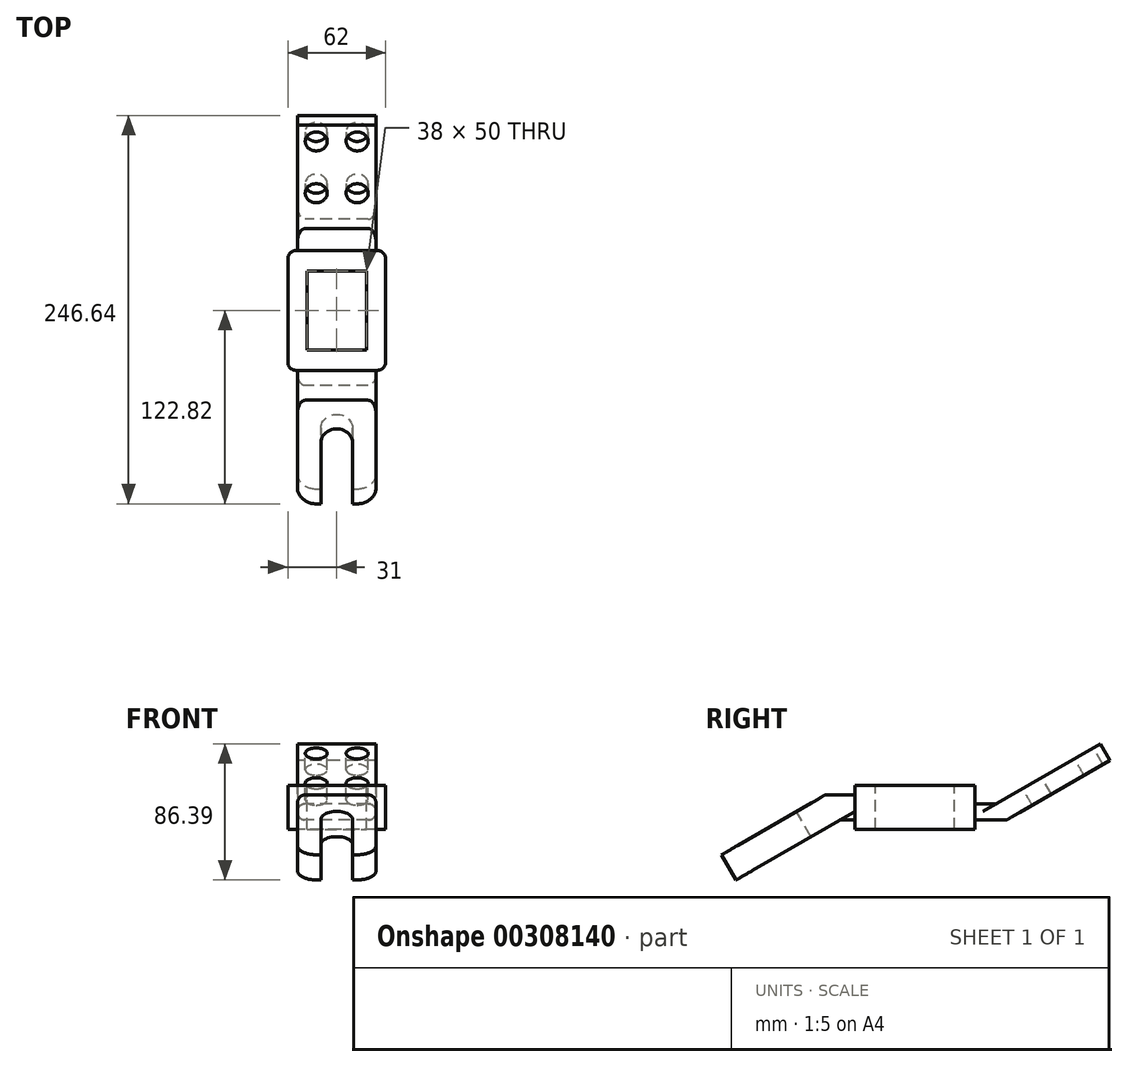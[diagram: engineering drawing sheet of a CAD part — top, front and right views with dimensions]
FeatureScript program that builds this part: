
annotation { "Feature Type Name" : "Feature", "Feature Type Description" : "" }
export const myFeature = defineFeature(function(context is Context, id is Id, definition is map)
    precondition{}
    {
        {
            var Q0;
            Q0=qCreatedBy(makeId("Right.planeOp"),FACE);
            var sketch = newSketch(context, id + "F0", { "sketchPlane" : qUnion([Q0])});
            skLineSegment(sketch, "E0.bottom", {"start": v(38, 14) * mm, "end": v(-38, 14) * mm});
            skLineSegment(sketch, "E0.top", {"start": v(38, -14) * mm, "end": v(-38, -14) * mm});
            skLineSegment(sketch, "E0.left", {"start": v(38, 14) * mm, "end": v(38, -14) * mm});
            skLineSegment(sketch, "E0.right", {"start": v(-38, 14) * mm, "end": v(-38, -14) * mm});
            skPoint(sketch, "E0.middle", {"position": v(0, 0) * mm});
            skLineSegment(sketch, "E1", {"start": v(-38, 8) * mm, "end": v(-57, 8) * mm});
            skLineSegment(sketch, "E2", {"start": v(-57, 8) * mm, "end": v(-122.82, -30) * mm});
            skLineSegment(sketch, "E3", {"start": v(-122.82, -30) * mm, "end": v(-113.58, -46) * mm});
            skLineSegment(sketch, "E4", {"start": v(38, -8) * mm, "end": v(58, -8) * mm});
            skLineSegment(sketch, "E5", {"start": v(58, -8) * mm, "end": v(123.82, 30) * mm});
            skLineSegment(sketch, "E6", {"start": v(123.82, 30) * mm, "end": v(117.82, 40.4) * mm});
            skLineSegment(sketch, "E7", {"start": v(117.82, 40.4) * mm, "end": v(52, 2.4) * mm});
            skLineSegment(sketch, "E8", {"start": v(-38, -8) * mm, "end": v(-47.76, -8) * mm});
            skLineSegment(sketch, "E9", {"start": v(-47.76, -8) * mm, "end": v(-113.58, -46) * mm});
            skLineSegment(sketch, "E10", {"start": v(52, 2.4) * mm, "end": v(38, 2.4) * mm});
            skSolve(sketch);
        }
        {
            var Q0;
            {var subQ3=sQuery(id+"F0.wireOp",EDGE,"E0.bottom");Q0=makeQuery(id+"F0.imprint","IMPRINT",FACE,{"disambiguationData":[TD([[makeQuery(id+"F0.imprint","IMPRINT",EDGE,{"derivedFrom":subQ3}),1.0]])]});}
            extrude(context, id + "F1", {"entities" : qUnion([Q0]), "endBound" : BoundingType.SYMMETRIC, "depth" : 62 * mm});
        }
        {
            var Q0;
            {var subQ0=sQuery(id+"F0.wireOp",EDGE,"E1");Q0=makeQuery(id+"F0.imprint","IMPRINT",FACE,{"disambiguationData":[TD([[makeQuery(id+"F0.imprint","IMPRINT",EDGE,{"derivedFrom":subQ0}),1.0]])]});}
            var Q1;
            {var subQ0=sQuery(id+"F0.wireOp",EDGE,"E4");Q1=makeQuery(id+"F0.imprint","IMPRINT",FACE,{"disambiguationData":[TD([[makeQuery(id+"F0.imprint","IMPRINT",EDGE,{"derivedFrom":subQ0}),1.0]])]});}
            extrude(context, id + "F2", {"entities" : qUnion([Q0, Q1]), "operationType" : NewBodyOperationType.ADD, "endBound" : BoundingType.SYMMETRIC, "depth" : 50 * mm});
        }
        {
            var Q0;
            Q0=makeQuery(id+"F2.opExtrude","SWEPT_FACE",FACE,{"disambiguationData":[OSD([sQuery(id+"F0.wireOp",EDGE,"E2")])]});
            var sketch = newSketch(context, id + "F3", { "sketchPlane" : qUnion([Q0])});
            skCircle(sketch, "E11", {"center": v(0, -76.36) * mm, "radius": 10 * mm});
            skLineSegment(sketch, "E12", {"start": v(-10, -76.36) * mm, "end": v(-10, -121.36) * mm});
            skLineSegment(sketch, "E13", {"start": v(10, -76.36) * mm, "end": v(10, -121.36) * mm});
            skSolve(sketch);
        }
        {
            var Q0;
            {var subQ0=sQuery(id+"F3.wireOp",EDGE,"E12");Q0=makeQuery(id+"F3.imprint","IMPRINT",FACE,{"disambiguationData":[TD([[makeQuery(id+"F3.imprint","IMPRINT",EDGE,{"derivedFrom":subQ0}),1.0]])]});}
            var Q1;
            {var subQ0=sQuery(id+"F3.wireOp",EDGE,"E11");var subQ1=makeQuery(id+"F3.imprint","INTERSECT",VERTEX,{"derivedFrom":[subQ0,sQuery(id+"F3.wireOp",EDGE,"E12")]});Q1=makeQuery(id+"F3.imprint","IMPRINT",FACE,{"disambiguationData":[TD([[makeQuery(id+"F3.imprint","IMPRINT",EDGE,{"disambiguationData":[TD([[subQ1,1.0]])],"derivedFrom":subQ0}),1.0]])]});}
            extrude(context, id + "F4", {"entities" : qUnion([Q0, Q1]), "operationType" : NewBodyOperationType.REMOVE, "endBound" : BoundingType.THROUGH_ALL, "oppositeDirection" : true, "depth" : 25 * mm});
        }
        {
            var Q0;
            Q0=makeQuery(id+"F2.opExtrude","CAP_EDGE",EDGE,{"disambiguationData":[OSD([sQuery(id+"F0.wireOp",EDGE,"E3")])],"isStart":false});
            var Q1;
            Q1=makeQuery(id+"F2.opExtrude","CAP_EDGE",EDGE,{"disambiguationData":[OSD([sQuery(id+"F0.wireOp",EDGE,"E3")])],"isStart":true});
            fillet(context, id + "F5", {"entities" : qUnion([Q0, Q1]), "radius" : 12 * mm, "tangentPropagation" : true, "allowEdgeOverflow" : false});
        }
        {
            var Q0;
            Q0=makeQuery(id+"F2.opExtrude","SWEPT_FACE",FACE,{"disambiguationData":[OSD([sQuery(id+"F0.wireOp",EDGE,"E7")])]});
            var sketch = newSketch(context, id + "F6", { "sketchPlane" : qUnion([Q0])});
            skCircle(sketch, "E14", {"center": v(-13, 110.23) * mm, "radius": 7 * mm});
            skCircle(sketch, "E15.0.1.0", {"center": v(-13, 72.23) * mm, "radius": 7 * mm});
            skCircle(sketch, "E15.1.0.0", {"center": v(13, 110.23) * mm, "radius": 7 * mm});
            skCircle(sketch, "E15.1.1.0", {"center": v(13, 72.23) * mm, "radius": 7 * mm});
            skLineSegment(sketch, "E15.direction1", {"start": v(-13, 110.23) * mm, "end": v(13, 110.23) * mm, "construction": true});
            skLineSegment(sketch, "E15.direction2", {"start": v(-13, 110.23) * mm, "end": v(-13, 72.23) * mm, "construction": true});
            skSolve(sketch);
        }
        {
            var Q0;
            Q0=makeQuery(id+"F6.imprint","IMPRINT",FACE,{"disambiguationData":[TD([[makeQuery(id+"F6.imprint","IMPRINT",EDGE,{"derivedFrom":sQuery(id+"F6.wireOp",EDGE,"E14")}),1.0]])]});
            var Q1;
            Q1=makeQuery(id+"F6.imprint","IMPRINT",FACE,{"disambiguationData":[TD([[makeQuery(id+"F6.imprint","IMPRINT",EDGE,{"derivedFrom":sQuery(id+"F6.wireOp",EDGE,"E15.1.0.0")}),1.0]])]});
            var Q2;
            Q2=makeQuery(id+"F6.imprint","IMPRINT",FACE,{"disambiguationData":[TD([[makeQuery(id+"F6.imprint","IMPRINT",EDGE,{"derivedFrom":sQuery(id+"F6.wireOp",EDGE,"E15.1.1.0")}),1.0]])]});
            var Q3;
            Q3=makeQuery(id+"F6.imprint","IMPRINT",FACE,{"disambiguationData":[TD([[makeQuery(id+"F6.imprint","IMPRINT",EDGE,{"derivedFrom":sQuery(id+"F6.wireOp",EDGE,"E15.0.1.0")}),1.0]])]});
            extrude(context, id + "F7", {"entities" : qUnion([Q0, Q1, Q2, Q3]), "operationType" : NewBodyOperationType.REMOVE, "endBound" : BoundingType.THROUGH_ALL, "oppositeDirection" : true, "depth" : 25 * mm});
        }
        {
            var Q0;
            Q0=makeQuery(id+"F1.opExtrude","SWEPT_FACE",FACE,{"disambiguationData":[OSD([sQuery(id+"F0.wireOp",EDGE,"E0.bottom")])]});
            var sketch = newSketch(context, id + "F8", { "sketchPlane" : qUnion([Q0])});
            skLineSegment(sketch, "E16.bottom", {"start": v(19, -25) * mm, "end": v(-19, -25) * mm});
            skLineSegment(sketch, "E16.top", {"start": v(19, 25) * mm, "end": v(-19, 25) * mm});
            skLineSegment(sketch, "E16.left", {"start": v(19, -25) * mm, "end": v(19, 25) * mm});
            skLineSegment(sketch, "E16.right", {"start": v(-19, -25) * mm, "end": v(-19, 25) * mm});
            skPoint(sketch, "E16.middle", {"position": v(0, 0) * mm});
            skSolve(sketch);
        }
        {
            var Q0;
            Q0=makeQuery(id+"F8.imprint","IMPRINT",FACE,{"disambiguationData":[TD([[makeQuery(id+"F8.imprint","IMPRINT",EDGE,{"derivedFrom":sQuery(id+"F8.wireOp",EDGE,"E16.bottom")}),-1.0]])]});
            extrude(context, id + "F9", {"entities" : qUnion([Q0]), "operationType" : NewBodyOperationType.REMOVE, "endBound" : BoundingType.THROUGH_ALL, "oppositeDirection" : true, "depth" : 25 * mm});
        }
        {
            var Q0;
            Q0=makeQuery(id+"F1.opExtrude","CAP_EDGE",EDGE,{"disambiguationData":[OSD([sQuery(id+"F0.wireOp",EDGE,"E0.right")])],"isStart":false});
            var Q1;
            Q1=makeQuery(id+"F1.opExtrude","CAP_EDGE",EDGE,{"disambiguationData":[OSD([sQuery(id+"F0.wireOp",EDGE,"E0.right")])],"isStart":true});
            var Q2;
            Q2=makeQuery(id+"F1.opExtrude","CAP_EDGE",EDGE,{"disambiguationData":[OSD([sQuery(id+"F0.wireOp",EDGE,"E0.left")])],"isStart":false});
            var Q3;
            Q3=makeQuery(id+"F1.opExtrude","CAP_EDGE",EDGE,{"disambiguationData":[OSD([sQuery(id+"F0.wireOp",EDGE,"E0.left")])],"isStart":true});
            var Q4;
            Q4=makeQuery(id+"F2.opExtrude","CAP_EDGE",EDGE,{"disambiguationData":[OSD([sQuery(id+"F0.wireOp",EDGE,"E1")])],"isStart":false});
            var Q5;
            Q5=makeQuery(id+"F2.opExtrude","CAP_EDGE",EDGE,{"disambiguationData":[OSD([sQuery(id+"F0.wireOp",EDGE,"E1")])],"isStart":true});
            var Q6;
            Q6=makeQuery(id+"F2.opExtrude","CAP_EDGE",EDGE,{"disambiguationData":[OSD([sQuery(id+"F0.wireOp",EDGE,"E10")])],"isStart":false});
            var Q7;
            Q7=makeQuery(id+"F2.opExtrude","CAP_EDGE",EDGE,{"disambiguationData":[OSD([sQuery(id+"F0.wireOp",EDGE,"E0.left")])],"isStart":false});
            var Q8;
            Q8=makeQuery(id+"F2.opExtrude","CAP_EDGE",EDGE,{"disambiguationData":[OSD([sQuery(id+"F0.wireOp",EDGE,"E10")])],"isStart":true});
            var Q9;
            Q9=makeQuery(id+"F2.opExtrude","CAP_EDGE",EDGE,{"disambiguationData":[OSD([sQuery(id+"F0.wireOp",EDGE,"E4")])],"isStart":false});
            var Q10;
            Q10=makeQuery(id+"F2.opExtrude","CAP_EDGE",EDGE,{"disambiguationData":[OSD([sQuery(id+"F0.wireOp",EDGE,"E8")])],"isStart":false});
            var Q11;
            Q11=makeQuery(id+"F2.opExtrude","CAP_EDGE",EDGE,{"disambiguationData":[OSD([sQuery(id+"F0.wireOp",EDGE,"E4")])],"isStart":true});
            var Q12;
            Q12=makeQuery(id+"F2.opExtrude","CAP_EDGE",EDGE,{"disambiguationData":[OSD([sQuery(id+"F0.wireOp",EDGE,"E8")])],"isStart":true});
            fillet(context, id + "F10", {"entities" : qUnion([Q0, Q1, Q2, Q3, Q4, Q5, Q6, Q7, Q8, Q9, Q10, Q11, Q12]), "radius" : 5 * mm, "tangentPropagation" : true, "allowEdgeOverflow" : false});
        }
    });
